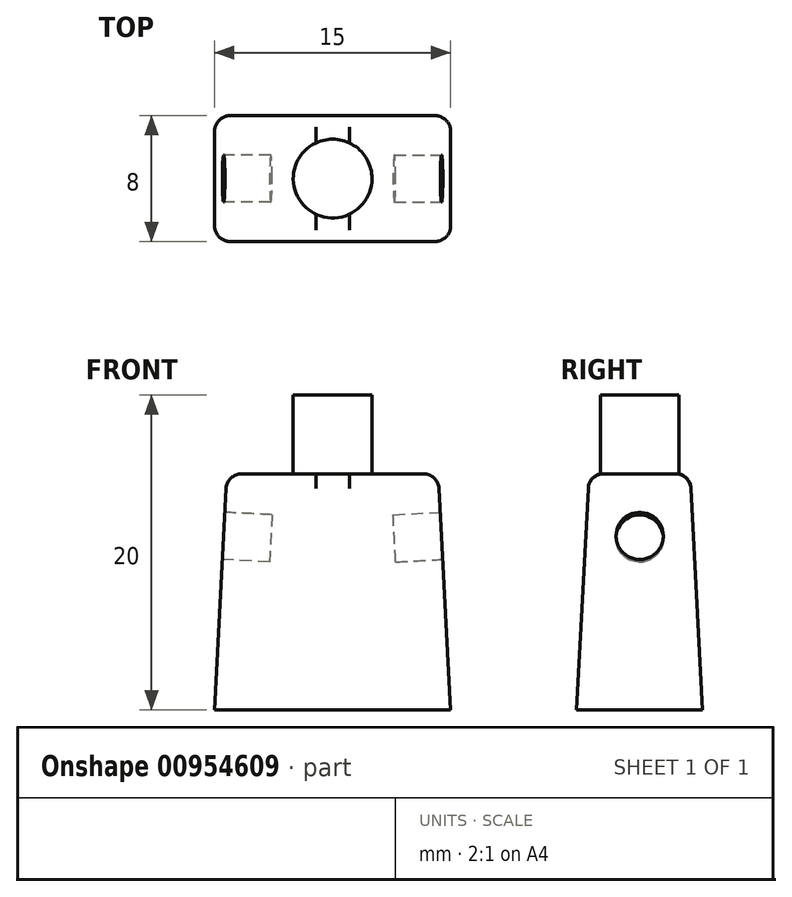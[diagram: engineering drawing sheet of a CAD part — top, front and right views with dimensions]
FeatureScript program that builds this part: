
annotation { "Feature Type Name" : "Feature", "Feature Type Description" : "" }
export const myFeature = defineFeature(function(context is Context, id is Id, definition is map)
    precondition{}
    {
        {
            var Q0;
            Q0=qCreatedBy(makeId("Top.planeOp"),FACE);
            var sketch = newSketch(context, id + "F0", { "sketchPlane" : qUnion([Q0])});
            skLineSegment(sketch, "E0.bottom", {"start": v(-7.5, 4) * mm, "end": v(7.5, 4) * mm});
            skLineSegment(sketch, "E0.top", {"start": v(-7.5, -4) * mm, "end": v(7.5, -4) * mm});
            skLineSegment(sketch, "E0.left", {"start": v(-7.5, 4) * mm, "end": v(-7.5, -4) * mm});
            skLineSegment(sketch, "E0.right", {"start": v(7.5, 4) * mm, "end": v(7.5, -4) * mm});
            skPoint(sketch, "E0.middle", {"position": v(0, 0) * mm});
            skSolve(sketch);
        }
        {
            var Q0;
            Q0 = qSketchRegion(id + "F0", true);
            extrude(context, id + "F1", {"entities" : qUnion([Q0]), "depth" : 15 * mm, "offsetDistance" : 25.4 * mm, "hasDraft" : true, "draftAngle" : 3 * degree, "draftPullDirection" : true});
        }
        {
            var Q0;
            Q0=makeQuery(id+"F1.opExtrude","CAP_FACE",FACE,{"disambiguationData":[OSD([sQuery(id+"F0.wireOp",EDGE,"E0.bottom"),sQuery(id+"F0.wireOp",EDGE,"E0.top"),sQuery(id+"F0.wireOp",EDGE,"E0.left"),sQuery(id+"F0.wireOp",EDGE,"E0.right")])],"isStart":false});
            var sketch = newSketch(context, id + "F2", { "sketchPlane" : qUnion([Q0])});
            skCircle(sketch, "E1", {"center": v(0, 0) * mm, "radius": 2.5 * mm});
            skSolve(sketch);
        }
        {
            var Q0;
            Q0 = qSketchRegion(id + "F2", true);
            extrude(context, id + "F3", {"entities" : qUnion([Q0]), "operationType" : NewBodyOperationType.ADD, "depth" : 5 * mm, "offsetDistance" : 25.4 * mm});
        }
        {
            var Q0;
            Q0=makeQuery(id+"F1.opExtrude","SWEPT_EDGE",EDGE,{"disambiguationData":[OSD([sQuery(id+"F0.wireOp",EDGE,"E0.bottom"),sQuery(id+"F0.wireOp",EDGE,"E0.left")])]});
            var Q1;
            Q1=makeQuery(id+"F1.opExtrude","SWEPT_EDGE",EDGE,{"disambiguationData":[OSD([sQuery(id+"F0.wireOp",EDGE,"E0.bottom"),sQuery(id+"F0.wireOp",EDGE,"E0.right")])]});
            var Q2;
            Q2=makeQuery(id+"F1.opExtrude","SWEPT_EDGE",EDGE,{"disambiguationData":[OSD([sQuery(id+"F0.wireOp",EDGE,"E0.top"),sQuery(id+"F0.wireOp",EDGE,"E0.left")])]});
            var Q3;
            Q3=makeQuery(id+"F1.opExtrude","CAP_EDGE",EDGE,{"disambiguationData":[OSD([sQuery(id+"F0.wireOp",EDGE,"E0.bottom")])],"isStart":false});
            var Q4;
            Q4=makeQuery(id+"F1.opExtrude","CAP_EDGE",EDGE,{"disambiguationData":[OSD([sQuery(id+"F0.wireOp",EDGE,"E0.left")])],"isStart":false});
            var Q5;
            Q5=makeQuery(id+"F1.opExtrude","CAP_EDGE",EDGE,{"disambiguationData":[OSD([sQuery(id+"F0.wireOp",EDGE,"E0.right")])],"isStart":false});
            var Q6;
            Q6=makeQuery(id+"F1.opExtrude","CAP_EDGE",EDGE,{"disambiguationData":[OSD([sQuery(id+"F0.wireOp",EDGE,"E0.top")])],"isStart":false});
            fillet(context, id + "F4", {"entities" : qUnion([Q0, Q1, Q2, Q3, Q4, Q5, Q6]), "radius" : 1 * mm, "tangentPropagation" : true, "allowEdgeOverflow" : false});
        }
        {
            var Q0;
            Q0=makeQuery(id+"F1.opExtrude","SWEPT_EDGE",EDGE,{"disambiguationData":[OSD([sQuery(id+"F0.wireOp",EDGE,"E0.top"),sQuery(id+"F0.wireOp",EDGE,"E0.right")])]});
            fillet(context, id + "F5", {"entities" : qUnion([Q0]), "radius" : 1 * mm, "tangentPropagation" : true, "allowEdgeOverflow" : false});
        }
        {
            var Q0;
            Q0=makeQuery(id+"F1.opExtrude","SWEPT_FACE",FACE,{"disambiguationData":[OSD([sQuery(id+"F0.wireOp",EDGE,"E0.right")])]});
            var sketch = newSketch(context, id + "F6", { "sketchPlane" : qUnion([Q0])});
            skCircle(sketch, "E2", {"center": v(0, 10.68) * mm, "radius": 1.5 * mm});
            skSolve(sketch);
        }
        {
            var Q0;
            Q0 = qSketchRegion(id + "F6", true);
            extrude(context, id + "F7", {"entities" : qUnion([Q0]), "operationType" : NewBodyOperationType.REMOVE, "oppositeDirection" : true, "depth" : 3 * mm, "offsetDistance" : 25.4 * mm});
        }
        {
            var Q0;
            Q0=makeQuery(id+"F1.opExtrude","SWEPT_FACE",FACE,{"disambiguationData":[OSD([sQuery(id+"F0.wireOp",EDGE,"E0.left")])]});
            var sketch = newSketch(context, id + "F8", { "sketchPlane" : qUnion([Q0])});
            skCircle(sketch, "E3", {"center": v(0, 10.68) * mm, "radius": 1.5 * mm});
            skSolve(sketch);
        }
        {
            var Q0;
            Q0 = qSketchRegion(id + "F8", true);
            extrude(context, id + "F9", {"entities" : qUnion([Q0]), "operationType" : NewBodyOperationType.REMOVE, "oppositeDirection" : true, "depth" : 3 * mm, "offsetDistance" : 25.4 * mm});
        }
    });
